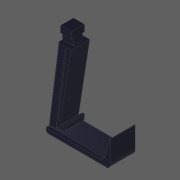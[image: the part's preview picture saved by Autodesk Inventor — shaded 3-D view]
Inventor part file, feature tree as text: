
AUTODESK INVENTOR PART (.ipt)
format: ipt  version: 2020 (Build 240168000, 168)  size: 262,144 bytes
history: native  units: in
note: dims shown in document units (in); Inventor stores cm internally (conversion verified against a paired STEP export)
features: fillet x5, other x3, extrude x3
ambient origin geometry x8: Origin, YZ Plane, XZ Plane, XY Plane, X Axis, Y Axis, Z Axis, Center Point
bodies: Solid1 (feature_tree)
feature tree (11):
  other  "Neck Start Plane"
  other  "Arm Profile"
  extrude  "Main Arm"  Depth=0.0039in
  extrude  "Pincher"  Depth=1.0386in
  extrude  "Neck"  Depth=0.7283in
  fillet  "Spring Hook Fillet"  Radius=0.1181in
  fillet  "Spring Attachment Fillet"  [1 undecoded]
  fillet  "Soft Edges"  Radius=0.195in
  fillet  "Pincher Fillet 1"  Radius=0.0197in
  fillet  "Pincher Fillet 2"  Radius=0.0394in
  other  "Neck Sketch"
note: 1 required parameter value undecoded (feature->parameter linkage not recoverable at this tier; creation-order binding heuristic only, values carry confidence <= 0.55)
